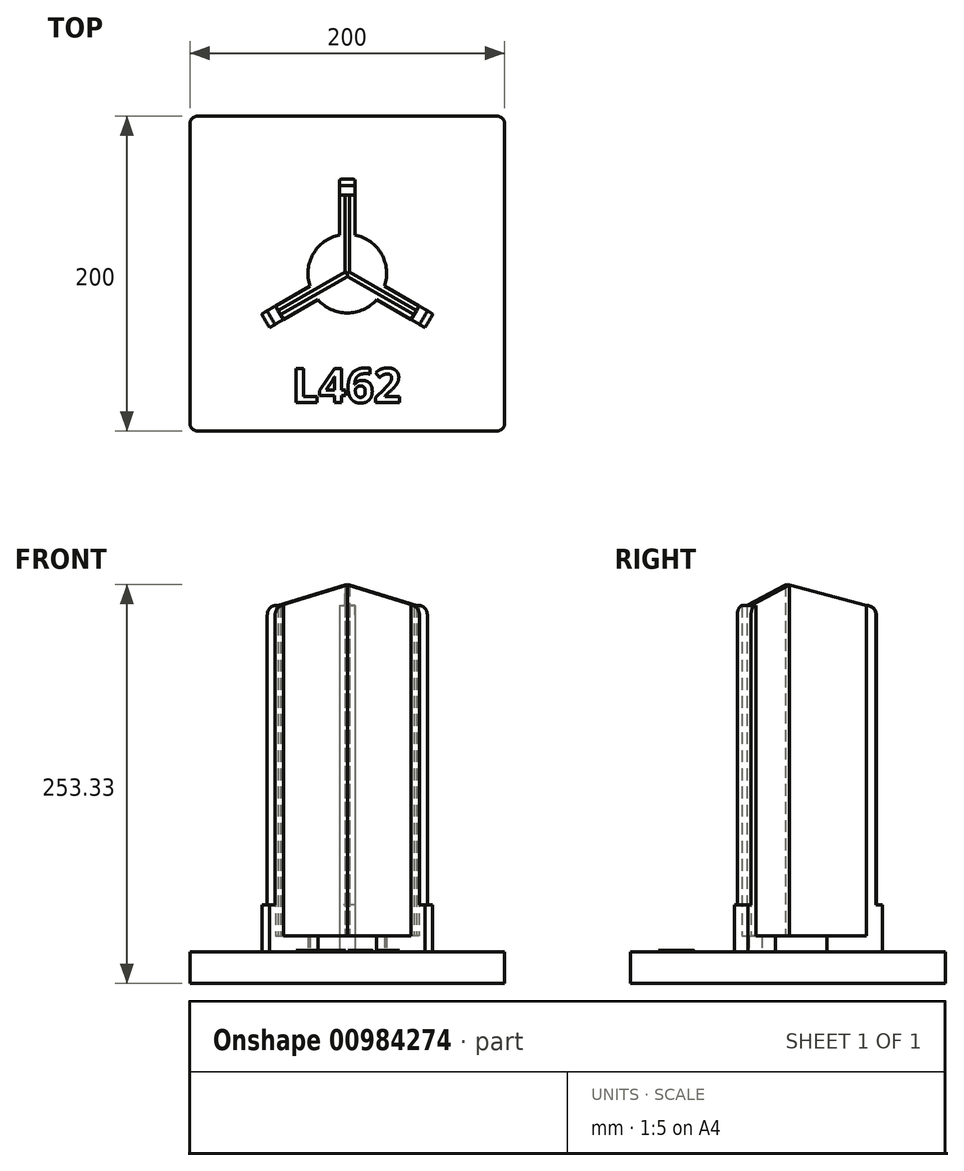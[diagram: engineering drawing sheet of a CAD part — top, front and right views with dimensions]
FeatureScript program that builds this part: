
annotation { "Feature Type Name" : "Feature", "Feature Type Description" : "" }
export const myFeature = defineFeature(function(context is Context, id is Id, definition is map)
    precondition{}
    {
        {
            var Q0;
            Q0=qCreatedBy(makeId("Top.planeOp"),FACE);
            var sketch = newSketch(context, id + "F0", { "sketchPlane" : qUnion([Q0])});
            skCircle(sketch, "E0", {"center": v(0, 0) * mm, "radius": 60 * mm});
            skCircle(sketch, "E1", {"center": v(0, 0) * mm, "radius": 56 * mm});
            skCircle(sketch, "E2", {"center": v(0, 0) * mm, "radius": 25 * mm});
            skLineSegment(sketch, "E3", {"start": v(-1.5, 55.98) * mm, "end": v(1.5, 55.98) * mm, "construction": true});
            skLineSegment(sketch, "E4", {"start": v(-5, 59.8) * mm, "end": v(5, 59.8) * mm, "construction": true});
            skCircle(sketch, "E5", {"center": v(0, 0) * mm, "radius": 1.5 * mm, "construction": true});
            skLineSegment(sketch, "E6", {"start": v(-1.5, 55.98) * mm, "end": v(-1.5, 0) * mm});
            skLineSegment(sketch, "E7", {"start": v(1.5, 55.98) * mm, "end": v(1.5, 0) * mm});
            skLineSegment(sketch, "E8", {"start": v(-5, 59.8) * mm, "end": v(-5, 55.78) * mm});
            skLineSegment(sketch, "E9", {"start": v(5, 59.8) * mm, "end": v(5, 55.78) * mm});
            skLineSegment(sketch, "E10", {"start": v(-1.5, 24.95) * mm, "end": v(-22.36, -11.18) * mm, "construction": true});
            skCircle(sketch, "E11", {"center": v(-11.93, 6.89) * mm, "radius": 3.5 * mm});
            skCircle(sketch, "E12", {"center": v(-11.93, 6.89) * mm, "radius": 1.75 * mm});
            skCircle(sketch, "E13.1.0", {"center": v(0, -13.78) * mm, "radius": 1.75 * mm});
            skCircle(sketch, "E13.1.1", {"center": v(0, -13.78) * mm, "radius": 3.5 * mm});
            skCircle(sketch, "E13.2.0", {"center": v(11.93, 6.89) * mm, "radius": 1.75 * mm});
            skCircle(sketch, "E13.2.1", {"center": v(11.93, 6.89) * mm, "radius": 3.5 * mm});
            skLineSegment(sketch, "E14", {"start": v(-5, 55.78) * mm, "end": v(-5, 24.5) * mm});
            skLineSegment(sketch, "E15", {"start": v(5, 55.78) * mm, "end": v(5, 24.5) * mm});
            skCircle(sketch, "E16", {"center": v(0, 0) * mm, "radius": 50 * mm, "construction": true});
            skLineSegment(sketch, "E17", {"start": v(-5, 49.75) * mm, "end": v(5, 49.75) * mm});
            skLineSegment(sketch, "E18.1.0", {"start": v(-47.73, -29.29) * mm, "end": v(0.75, -1.3) * mm});
            skLineSegment(sketch, "E18.1.1", {"start": v(-49.23, -26.7) * mm, "end": v(-0.75, 1.3) * mm});
            skLineSegment(sketch, "E18.1.2", {"start": v(-45.8, -32.22) * mm, "end": v(-18.71, -16.58) * mm});
            skLineSegment(sketch, "E18.1.3", {"start": v(-50.8, -23.56) * mm, "end": v(-23.71, -7.92) * mm});
            skLineSegment(sketch, "E18.1.4", {"start": v(-49.28, -34.23) * mm, "end": v(-45.8, -32.22) * mm});
            skLineSegment(sketch, "E18.1.5", {"start": v(-54.28, -25.57) * mm, "end": v(-50.8, -23.56) * mm});
            skLineSegment(sketch, "E18.1.6", {"start": v(-49.28, -34.23) * mm, "end": v(-54.28, -25.57) * mm, "construction": true});
            skLineSegment(sketch, "E18.1.7", {"start": v(-47.73, -29.29) * mm, "end": v(-49.23, -26.7) * mm, "construction": true});
            skLineSegment(sketch, "E18.1.8", {"start": v(-40.58, -29.2) * mm, "end": v(-45.58, -20.54) * mm});
            skLineSegment(sketch, "E18.2.0", {"start": v(49.23, -26.7) * mm, "end": v(0.75, 1.3) * mm});
            skLineSegment(sketch, "E18.2.1", {"start": v(47.73, -29.29) * mm, "end": v(-0.75, -1.3) * mm});
            skLineSegment(sketch, "E18.2.2", {"start": v(50.8, -23.56) * mm, "end": v(23.71, -7.92) * mm});
            skLineSegment(sketch, "E18.2.3", {"start": v(45.8, -32.22) * mm, "end": v(18.71, -16.58) * mm});
            skLineSegment(sketch, "E18.2.4", {"start": v(54.28, -25.57) * mm, "end": v(50.8, -23.56) * mm});
            skLineSegment(sketch, "E18.2.5", {"start": v(49.28, -34.23) * mm, "end": v(45.8, -32.22) * mm});
            skLineSegment(sketch, "E18.2.6", {"start": v(54.28, -25.57) * mm, "end": v(49.28, -34.23) * mm, "construction": true});
            skLineSegment(sketch, "E18.2.7", {"start": v(49.23, -26.7) * mm, "end": v(47.73, -29.29) * mm, "construction": true});
            skLineSegment(sketch, "E18.2.8", {"start": v(45.58, -20.54) * mm, "end": v(40.58, -29.2) * mm});
            skText(sketch, "E19", { "text": "L462", "fontName": "OpenSans-Bold.ttf"});
            const initialGuessF0  = {"E19": [-0.0353, -0.082, 1, 0, 0.022]};
            skSetInitialGuess(sketch, initialGuessF0);
            skSolve(sketch);
        }
        {
            var Q0;
            {var subQ0=sQuery(id+"F0.wireOp",EDGE,"E2");var subQ1=sQuery(id+"F0.wireOp",EDGE,"Qz9RoNIK-bmAM-g4SH-EP3c-7Fqs6VSRPzqB.left");var subQ2=makeQuery(id+"F0.imprint","INTERSECT",VERTEX,{"disambiguationData":[OD(0.0)],"derivedFrom":[subQ1,subQ0]});Q0=makeQuery(id+"F0.imprint","IMPRINT",FACE,{"disambiguationData":[TD([[makeQuery(id+"F0.imprint","IMPRINT",EDGE,{"disambiguationData":[TD([[subQ2,-1.0]])],"derivedFrom":subQ1}),1.0]])]});}
            var Q1;
            {var subQ0=sQuery(id+"F0.wireOp",EDGE,"E2");var subQ1=sQuery(id+"F0.wireOp",EDGE,"Qz9RoNIK-bmAM-g4SH-EP3c-7Fqs6VSRPzqB.left");var subQ2=makeQuery(id+"F0.imprint","INTERSECT",VERTEX,{"disambiguationData":[OD(0.0)],"derivedFrom":[subQ1,subQ0]});Q1=makeQuery(id+"F0.imprint","IMPRINT",FACE,{"disambiguationData":[TD([[makeQuery(id+"F0.imprint","IMPRINT",EDGE,{"disambiguationData":[TD([[subQ2,-1.0]])],"derivedFrom":subQ1}),-1.0]])]});}
            var Q2;
            {var subQ1=sQuery(id+"F0.wireOp",EDGE,"Qz9RoNIK-bmAM-g4SH-EP3c-7Fqs6VSRPzqB.right");var subQ5=sQuery(id+"F0.wireOp",EDGE,"E2");var subQ6=makeQuery(id+"F0.imprint","INTERSECT",VERTEX,{"disambiguationData":[OD(0.0)],"derivedFrom":[subQ1,subQ5]});Q2=makeQuery(id+"F0.imprint","IMPRINT",FACE,{"disambiguationData":[TD([[makeQuery(id+"F0.imprint","IMPRINT",EDGE,{"disambiguationData":[TD([[subQ6,-1.0]])],"derivedFrom":subQ1}),-1.0]])]});}
            var Q3;
            {var subQ5=sQuery(id+"F0.wireOp",EDGE,"Qz9RoNIK-bmAM-g4SH-EP3c-7Fqs6VSRPzqB.right");var subQ7=sQuery(id+"F0.wireOp",EDGE,"I0Sq5aEr-Hngn-Fm4D-tp8S-rX2HjxpjUaP6.bottom");var subQ8=makeQuery(id+"F0.imprint","INTERSECT",VERTEX,{"derivedFrom":[subQ5,subQ7]});Q3=makeQuery(id+"F0.imprint","IMPRINT",FACE,{"disambiguationData":[TD([[makeQuery(id+"F0.imprint","IMPRINT",EDGE,{"disambiguationData":[TD([[subQ8,-1.0]])],"derivedFrom":subQ5}),-1.0]])]});}
            var Q4;
            {var subQ0=sQuery(id+"F0.wireOp",EDGE,"I0Sq5aEr-Hngn-Fm4D-tp8S-rX2HjxpjUaP6.bottom");var subQ1=sQuery(id+"F0.wireOp",EDGE,"Qz9RoNIK-bmAM-g4SH-EP3c-7Fqs6VSRPzqB.left");var subQ2=makeQuery(id+"F0.imprint","INTERSECT",VERTEX,{"derivedFrom":[subQ1,subQ0]});Q4=makeQuery(id+"F0.imprint","IMPRINT",FACE,{"disambiguationData":[TD([[makeQuery(id+"F0.imprint","IMPRINT",EDGE,{"disambiguationData":[TD([[subQ2,-1.0]])],"derivedFrom":subQ1}),-1.0]])]});}
            var Q5;
            {var subQ5=sQuery(id+"F0.wireOp",EDGE,"Qz9RoNIK-bmAM-g4SH-EP3c-7Fqs6VSRPzqB.left");var subQ7=sQuery(id+"F0.wireOp",EDGE,"I0Sq5aEr-Hngn-Fm4D-tp8S-rX2HjxpjUaP6.bottom");var subQ8=makeQuery(id+"F0.imprint","INTERSECT",VERTEX,{"derivedFrom":[subQ5,subQ7]});Q5=makeQuery(id+"F0.imprint","IMPRINT",FACE,{"disambiguationData":[TD([[makeQuery(id+"F0.imprint","IMPRINT",EDGE,{"disambiguationData":[TD([[subQ8,-1.0]])],"derivedFrom":subQ5}),1.0]])]});}
            var Q6;
            {var subQ0=sQuery(id+"F0.wireOp",EDGE,"MHhcaKt2-idaq-ussF-yxv1-Ysw6X7YejIML.top");var subQ1=sQuery(id+"F0.wireOp",EDGE,"Qz9RoNIK-bmAM-g4SH-EP3c-7Fqs6VSRPzqB.left");var subQ2=makeQuery(id+"F0.imprint","INTERSECT",VERTEX,{"derivedFrom":[subQ1,subQ0]});Q6=makeQuery(id+"F0.imprint","IMPRINT",FACE,{"disambiguationData":[TD([[makeQuery(id+"F0.imprint","IMPRINT",EDGE,{"disambiguationData":[TD([[subQ2,-1.0]])],"derivedFrom":subQ1}),1.0]])]});}
            var Q7;
            {var subQ0=sQuery(id+"F0.wireOp",EDGE,"MHhcaKt2-idaq-ussF-yxv1-Ysw6X7YejIML.top");var subQ1=sQuery(id+"F0.wireOp",EDGE,"Qz9RoNIK-bmAM-g4SH-EP3c-7Fqs6VSRPzqB.left");var subQ2=makeQuery(id+"F0.imprint","INTERSECT",VERTEX,{"derivedFrom":[subQ1,subQ0]});Q7=makeQuery(id+"F0.imprint","IMPRINT",FACE,{"disambiguationData":[TD([[makeQuery(id+"F0.imprint","IMPRINT",EDGE,{"disambiguationData":[TD([[subQ2,-1.0]])],"derivedFrom":subQ1}),-1.0]])]});}
            var Q8;
            {var subQ0=sQuery(id+"F0.wireOp",EDGE,"MHhcaKt2-idaq-ussF-yxv1-Ysw6X7YejIML.top");var subQ1=sQuery(id+"F0.wireOp",EDGE,"Qz9RoNIK-bmAM-g4SH-EP3c-7Fqs6VSRPzqB.right");var subQ2=makeQuery(id+"F0.imprint","INTERSECT",VERTEX,{"derivedFrom":[subQ1,subQ0]});Q8=makeQuery(id+"F0.imprint","IMPRINT",FACE,{"disambiguationData":[TD([[makeQuery(id+"F0.imprint","IMPRINT",EDGE,{"disambiguationData":[TD([[subQ2,-1.0]])],"derivedFrom":subQ1}),-1.0]])]});}
            var Q9;
            {var subQ0=sQuery(id+"F0.wireOp",EDGE,"I0Sq5aEr-Hngn-Fm4D-tp8S-rX2HjxpjUaP6.right");var subQ1=sQuery(id+"F0.wireOp",EDGE,"MHhcaKt2-idaq-ussF-yxv1-Ysw6X7YejIML.bottom");var subQ2=makeQuery(id+"F0.imprint","INTERSECT",VERTEX,{"derivedFrom":[subQ1,subQ0]});Q9=makeQuery(id+"F0.imprint","IMPRINT",FACE,{"disambiguationData":[TD([[makeQuery(id+"F0.imprint","IMPRINT",EDGE,{"disambiguationData":[TD([[subQ2,-1.0]])],"derivedFrom":subQ1}),-1.0]])]});}
            var Q10;
            {var subQ0=sQuery(id+"F0.wireOp",EDGE,"I0Sq5aEr-Hngn-Fm4D-tp8S-rX2HjxpjUaP6.top");var subQ1=sQuery(id+"F0.wireOp",EDGE,"Qz9RoNIK-bmAM-g4SH-EP3c-7Fqs6VSRPzqB.right");var subQ2=makeQuery(id+"F0.imprint","INTERSECT",VERTEX,{"derivedFrom":[subQ1,subQ0]});Q10=makeQuery(id+"F0.imprint","IMPRINT",FACE,{"disambiguationData":[TD([[makeQuery(id+"F0.imprint","IMPRINT",EDGE,{"disambiguationData":[TD([[subQ2,-1.0]])],"derivedFrom":subQ1}),-1.0]])]});}
            var Q11;
            {var subQ1=sQuery(id+"F0.wireOp",EDGE,"MHhcaKt2-idaq-ussF-yxv1-Ysw6X7YejIML.bottom");var subQ7=sQuery(id+"F0.wireOp",EDGE,"Qz9RoNIK-bmAM-g4SH-EP3c-7Fqs6VSRPzqB.right");var subQ8=makeQuery(id+"F0.imprint","INTERSECT",VERTEX,{"derivedFrom":[subQ7,subQ1]});Q11=makeQuery(id+"F0.imprint","IMPRINT",FACE,{"disambiguationData":[TD([[makeQuery(id+"F0.imprint","IMPRINT",EDGE,{"disambiguationData":[TD([[subQ8,-1.0]])],"derivedFrom":subQ7}),-1.0]])]});}
            var Q12;
            {var subQ0=sQuery(id+"F0.wireOp",EDGE,"MHhcaKt2-idaq-ussF-yxv1-Ysw6X7YejIML.bottom");var subQ1=sQuery(id+"F0.wireOp",EDGE,"Qz9RoNIK-bmAM-g4SH-EP3c-7Fqs6VSRPzqB.left");var subQ2=makeQuery(id+"F0.imprint","INTERSECT",VERTEX,{"derivedFrom":[subQ1,subQ0]});Q12=makeQuery(id+"F0.imprint","IMPRINT",FACE,{"disambiguationData":[TD([[makeQuery(id+"F0.imprint","IMPRINT",EDGE,{"disambiguationData":[TD([[subQ2,-1.0]])],"derivedFrom":subQ1}),-1.0]])]});}
            var Q13;
            {var subQ1=sQuery(id+"F0.wireOp",EDGE,"MHhcaKt2-idaq-ussF-yxv1-Ysw6X7YejIML.bottom");var subQ7=sQuery(id+"F0.wireOp",EDGE,"Qz9RoNIK-bmAM-g4SH-EP3c-7Fqs6VSRPzqB.left");var subQ8=makeQuery(id+"F0.imprint","INTERSECT",VERTEX,{"derivedFrom":[subQ7,subQ1]});Q13=makeQuery(id+"F0.imprint","IMPRINT",FACE,{"disambiguationData":[TD([[makeQuery(id+"F0.imprint","IMPRINT",EDGE,{"disambiguationData":[TD([[subQ8,-1.0]])],"derivedFrom":subQ7}),1.0]])]});}
            var Q14;
            {var subQ0=sQuery(id+"F0.wireOp",EDGE,"I0Sq5aEr-Hngn-Fm4D-tp8S-rX2HjxpjUaP6.top");var subQ1=sQuery(id+"F0.wireOp",EDGE,"Qz9RoNIK-bmAM-g4SH-EP3c-7Fqs6VSRPzqB.left");var subQ2=makeQuery(id+"F0.imprint","INTERSECT",VERTEX,{"derivedFrom":[subQ1,subQ0]});Q14=makeQuery(id+"F0.imprint","IMPRINT",FACE,{"disambiguationData":[TD([[makeQuery(id+"F0.imprint","IMPRINT",EDGE,{"disambiguationData":[TD([[subQ2,-1.0]])],"derivedFrom":subQ1}),1.0]])]});}
            var Q15;
            {var subQ0=sQuery(id+"F0.wireOp",EDGE,"E2");var subQ1=sQuery(id+"F0.wireOp",EDGE,"MHhcaKt2-idaq-ussF-yxv1-Ysw6X7YejIML.bottom");var subQ2=makeQuery(id+"F0.imprint","INTERSECT",VERTEX,{"disambiguationData":[OD(0.0)],"derivedFrom":[subQ1,subQ0]});Q15=makeQuery(id+"F0.imprint","IMPRINT",FACE,{"disambiguationData":[TD([[makeQuery(id+"F0.imprint","IMPRINT",EDGE,{"disambiguationData":[TD([[subQ2,-1.0]])],"derivedFrom":subQ1}),-1.0]])]});}
            var Q16;
            {var subQ0=sQuery(id+"F0.wireOp",EDGE,"I0Sq5aEr-Hngn-Fm4D-tp8S-rX2HjxpjUaP6.top");var subQ1=sQuery(id+"F0.wireOp",EDGE,"Qz9RoNIK-bmAM-g4SH-EP3c-7Fqs6VSRPzqB.left");var subQ2=makeQuery(id+"F0.imprint","INTERSECT",VERTEX,{"derivedFrom":[subQ1,subQ0]});Q16=makeQuery(id+"F0.imprint","IMPRINT",FACE,{"disambiguationData":[TD([[makeQuery(id+"F0.imprint","IMPRINT",EDGE,{"disambiguationData":[TD([[subQ2,-1.0]])],"derivedFrom":subQ1}),-1.0]])]});}
            var Q17;
            {var subQ0=sQuery(id+"F0.wireOp",EDGE,"ARnEnpE5-tkmW-Q9Fp-N7HQ-ZdpaRJQSmeqH.top");Q17=makeQuery(id+"F0.imprint","IMPRINT",FACE,{"disambiguationData":[TD([[makeQuery(id+"F0.imprint","IMPRINT",EDGE,{"derivedFrom":subQ0}),1.0]])]});}
            var Q18;
            {var subQ0=sQuery(id+"F0.wireOp",EDGE,"fYTYB3PY-5dvC-i0FG-IhBz-imLdNv0oFj73.right");Q18=makeQuery(id+"F0.imprint","IMPRINT",FACE,{"disambiguationData":[TD([[makeQuery(id+"F0.imprint","IMPRINT",EDGE,{"derivedFrom":subQ0}),-1.0]])]});}
            var Q19;
            {var subQ0=sQuery(id+"F0.wireOp",EDGE,"JRACFuVa-LFQl-MoOF-o5kD-FoGYgOgg0vGQ.top");Q19=makeQuery(id+"F0.imprint","IMPRINT",FACE,{"disambiguationData":[TD([[makeQuery(id+"F0.imprint","IMPRINT",EDGE,{"derivedFrom":subQ0}),-1.0]])]});}
            var Q20;
            {var subQ0=sQuery(id+"F0.wireOp",EDGE,"qvxIDn41-u5vC-3tcf-A1ba-gfAf9TCSAjBw.right");Q20=makeQuery(id+"F0.imprint","IMPRINT",FACE,{"disambiguationData":[TD([[makeQuery(id+"F0.imprint","IMPRINT",EDGE,{"derivedFrom":subQ0}),1.0]])]});}
            var Q21;
            {var subQ0=sQuery(id+"F0.wireOp",EDGE,"E2");var subQ1=sQuery(id+"F0.wireOp",EDGE,"Qz9RoNIK-bmAM-g4SH-EP3c-7Fqs6VSRPzqB.right");var subQ2=makeQuery(id+"F0.imprint","INTERSECT",VERTEX,{"disambiguationData":[OD(0.0)],"derivedFrom":[subQ1,subQ0]});Q21=makeQuery(id+"F0.imprint","IMPRINT",FACE,{"disambiguationData":[TD([[makeQuery(id+"F0.imprint","IMPRINT",EDGE,{"disambiguationData":[TD([[subQ2,-1.0]])],"derivedFrom":subQ1}),1.0]])]});}
            var Q22;
            {var subQ0=sQuery(id+"F0.wireOp",EDGE,"I0Sq5aEr-Hngn-Fm4D-tp8S-rX2HjxpjUaP6.bottom");var subQ1=sQuery(id+"F0.wireOp",EDGE,"Qz9RoNIK-bmAM-g4SH-EP3c-7Fqs6VSRPzqB.right");var subQ2=makeQuery(id+"F0.imprint","INTERSECT",VERTEX,{"derivedFrom":[subQ1,subQ0]});Q22=makeQuery(id+"F0.imprint","IMPRINT",FACE,{"disambiguationData":[TD([[makeQuery(id+"F0.imprint","IMPRINT",EDGE,{"disambiguationData":[TD([[subQ2,-1.0]])],"derivedFrom":subQ1}),1.0]])]});}
            var Q23;
            {var subQ0=sQuery(id+"F0.wireOp",EDGE,"MHhcaKt2-idaq-ussF-yxv1-Ysw6X7YejIML.top");var subQ1=sQuery(id+"F0.wireOp",EDGE,"Qz9RoNIK-bmAM-g4SH-EP3c-7Fqs6VSRPzqB.right");var subQ2=makeQuery(id+"F0.imprint","INTERSECT",VERTEX,{"derivedFrom":[subQ1,subQ0]});Q23=makeQuery(id+"F0.imprint","IMPRINT",FACE,{"disambiguationData":[TD([[makeQuery(id+"F0.imprint","IMPRINT",EDGE,{"disambiguationData":[TD([[subQ2,-1.0]])],"derivedFrom":subQ1}),1.0]])]});}
            var Q24;
            {var subQ0=sQuery(id+"F0.wireOp",EDGE,"I0Sq5aEr-Hngn-Fm4D-tp8S-rX2HjxpjUaP6.right");var subQ1=sQuery(id+"F0.wireOp",EDGE,"MHhcaKt2-idaq-ussF-yxv1-Ysw6X7YejIML.top");var subQ2=makeQuery(id+"F0.imprint","INTERSECT",VERTEX,{"derivedFrom":[subQ1,subQ0]});Q24=makeQuery(id+"F0.imprint","IMPRINT",FACE,{"disambiguationData":[TD([[makeQuery(id+"F0.imprint","IMPRINT",EDGE,{"disambiguationData":[TD([[subQ2,-1.0]])],"derivedFrom":subQ1}),1.0]])]});}
            var Q25;
            {var subQ0=sQuery(id+"F0.wireOp",EDGE,"MHhcaKt2-idaq-ussF-yxv1-Ysw6X7YejIML.bottom");var subQ1=sQuery(id+"F0.wireOp",EDGE,"Qz9RoNIK-bmAM-g4SH-EP3c-7Fqs6VSRPzqB.right");var subQ2=makeQuery(id+"F0.imprint","INTERSECT",VERTEX,{"derivedFrom":[subQ1,subQ0]});Q25=makeQuery(id+"F0.imprint","IMPRINT",FACE,{"disambiguationData":[TD([[makeQuery(id+"F0.imprint","IMPRINT",EDGE,{"disambiguationData":[TD([[subQ2,-1.0]])],"derivedFrom":subQ1}),1.0]])]});}
            var Q26;
            {var subQ0=sQuery(id+"F0.wireOp",EDGE,"I0Sq5aEr-Hngn-Fm4D-tp8S-rX2HjxpjUaP6.top");var subQ1=sQuery(id+"F0.wireOp",EDGE,"Qz9RoNIK-bmAM-g4SH-EP3c-7Fqs6VSRPzqB.right");var subQ2=makeQuery(id+"F0.imprint","INTERSECT",VERTEX,{"derivedFrom":[subQ1,subQ0]});Q26=makeQuery(id+"F0.imprint","IMPRINT",FACE,{"disambiguationData":[TD([[makeQuery(id+"F0.imprint","IMPRINT",EDGE,{"disambiguationData":[TD([[subQ2,-1.0]])],"derivedFrom":subQ1}),1.0]])]});}
            var Q27;
            {var subQ0=sQuery(id+"F0.wireOp",EDGE,"UooLEnTI-Uf4f-MH2r-6JwD-Mf36DO2BtYOc.top");var subQ1=sQuery(id+"F0.wireOp",EDGE,"Qz9RoNIK-bmAM-g4SH-EP3c-7Fqs6VSRPzqB.right");var subQ2=makeQuery(id+"F0.imprint","INTERSECT",VERTEX,{"derivedFrom":[subQ1,subQ0]});Q27=makeQuery(id+"F0.imprint","IMPRINT",FACE,{"disambiguationData":[TD([[makeQuery(id+"F0.imprint","IMPRINT",EDGE,{"disambiguationData":[TD([[subQ2,-1.0]])],"derivedFrom":subQ1}),-1.0]])]});}
            var Q28;
            {var subQ0=sQuery(id+"F0.wireOp",EDGE,"UooLEnTI-Uf4f-MH2r-6JwD-Mf36DO2BtYOc.top");var subQ1=sQuery(id+"F0.wireOp",EDGE,"Qz9RoNIK-bmAM-g4SH-EP3c-7Fqs6VSRPzqB.right");var subQ2=makeQuery(id+"F0.imprint","INTERSECT",VERTEX,{"derivedFrom":[subQ1,subQ0]});Q28=makeQuery(id+"F0.imprint","IMPRINT",FACE,{"disambiguationData":[TD([[makeQuery(id+"F0.imprint","IMPRINT",EDGE,{"disambiguationData":[TD([[subQ2,-1.0]])],"derivedFrom":subQ1}),1.0]])]});}
            var Q29;
            {var subQ0=sQuery(id+"F0.wireOp",EDGE,"UooLEnTI-Uf4f-MH2r-6JwD-Mf36DO2BtYOc.top");var subQ1=sQuery(id+"F0.wireOp",EDGE,"Qz9RoNIK-bmAM-g4SH-EP3c-7Fqs6VSRPzqB.left");var subQ2=makeQuery(id+"F0.imprint","INTERSECT",VERTEX,{"derivedFrom":[subQ1,subQ0]});Q29=makeQuery(id+"F0.imprint","IMPRINT",FACE,{"disambiguationData":[TD([[makeQuery(id+"F0.imprint","IMPRINT",EDGE,{"disambiguationData":[TD([[subQ2,-1.0]])],"derivedFrom":subQ1}),-1.0]])]});}
            var Q30;
            {var subQ0=sQuery(id+"F0.wireOp",EDGE,"UooLEnTI-Uf4f-MH2r-6JwD-Mf36DO2BtYOc.top");var subQ1=sQuery(id+"F0.wireOp",EDGE,"Qz9RoNIK-bmAM-g4SH-EP3c-7Fqs6VSRPzqB.left");var subQ2=makeQuery(id+"F0.imprint","INTERSECT",VERTEX,{"derivedFrom":[subQ1,subQ0]});Q30=makeQuery(id+"F0.imprint","IMPRINT",FACE,{"disambiguationData":[TD([[makeQuery(id+"F0.imprint","IMPRINT",EDGE,{"disambiguationData":[TD([[subQ2,-1.0]])],"derivedFrom":subQ1}),1.0]])]});}
            var Q31;
            {var subQ0=sQuery(id+"F0.wireOp",EDGE,"E2");var subQ1=sQuery(id+"F0.wireOp",EDGE,"MHhcaKt2-idaq-ussF-yxv1-Ysw6X7YejIML.top");var subQ2=makeQuery(id+"F0.imprint","INTERSECT",VERTEX,{"disambiguationData":[OD(0.0)],"derivedFrom":[subQ1,subQ0]});Q31=makeQuery(id+"F0.imprint","IMPRINT",FACE,{"disambiguationData":[TD([[makeQuery(id+"F0.imprint","IMPRINT",EDGE,{"disambiguationData":[TD([[subQ2,-1.0]])],"derivedFrom":subQ1}),1.0]])]});}
            var Q32;
            {var subQ0=sQuery(id+"F0.wireOp",EDGE,"UaoCu7b1-m9SB-61mE-joAU-4Tf4ClvXxRAN");var subQ4=sQuery(id+"F0.wireOp",EDGE,"Z93t4qtu-qqve-2JoU-aCnr-fMp0EEGuzRtp");var subQ5=makeQuery(id+"F0.imprint","INTERSECT",VERTEX,{"disambiguationData":[OD(0.0)],"derivedFrom":[subQ4,subQ0]});Q32=makeQuery(id+"F0.imprint","IMPRINT",FACE,{"disambiguationData":[TD([[makeQuery(id+"F0.imprint","IMPRINT",EDGE,{"disambiguationData":[TD([[subQ5,1.0]])],"derivedFrom":subQ4}),-1.0]])]});}
            var Q33;
            Q33=makeQuery(id+"F0.imprint","IMPRINT",FACE,{"disambiguationData":[TD([[makeQuery(id+"F0.imprint","IMPRINT",EDGE,{"derivedFrom":sQuery(id+"F0.wireOp",EDGE,"3ba069c8-a511-4e33-be52-923c701046d1.1.1")}),-1.0]])]});
            var Q34;
            {var subQ5=sQuery(id+"F0.wireOp",EDGE,"3ec345ef-f0f0-4e93-9e5e-b6a35eb55933.1.2");var subQ6=sQuery(id+"F0.wireOp",EDGE,"E2");var subQ7=makeQuery(id+"F0.imprint","INTERSECT",VERTEX,{"derivedFrom":[subQ6,subQ5]});Q34=makeQuery(id+"F0.imprint","IMPRINT",FACE,{"disambiguationData":[TD([[makeQuery(id+"F0.imprint","IMPRINT",EDGE,{"disambiguationData":[TD([[subQ7,-1.0]])],"derivedFrom":subQ6}),1.0]])]});}
            var Q35;
            {var subQ1=sQuery(id+"F0.wireOp",EDGE,"E2");var subQ7=sQuery(id+"F0.wireOp",EDGE,"3ec345ef-f0f0-4e93-9e5e-b6a35eb55933.2.6");var subQ9=makeQuery(id+"F0.imprint","INTERSECT",VERTEX,{"derivedFrom":[subQ1,subQ7]});Q35=makeQuery(id+"F0.imprint","IMPRINT",FACE,{"disambiguationData":[TD([[makeQuery(id+"F0.imprint","IMPRINT",EDGE,{"disambiguationData":[TD([[subQ9,-1.0]])],"derivedFrom":subQ1}),1.0]])]});}
            var Q36;
            {var subQ1=sQuery(id+"F0.wireOp",EDGE,"Qz9RoNIK-bmAM-g4SH-EP3c-7Fqs6VSRPzqB.left");var subQ5=sQuery(id+"F0.wireOp",EDGE,"Fhyrr48q-6Ub6-qUJE-WvSH-lKAYv9wGpefs");var subQ6=makeQuery(id+"F0.imprint","INTERSECT",VERTEX,{"derivedFrom":[subQ1,subQ5]});Q36=makeQuery(id+"F0.imprint","IMPRINT",FACE,{"disambiguationData":[TD([[makeQuery(id+"F0.imprint","IMPRINT",EDGE,{"disambiguationData":[TD([[subQ6,1.0]])],"derivedFrom":subQ1}),1.0]])]});}
            var Q37;
            {var subQ0=sQuery(id+"F0.wireOp",EDGE,"Fhyrr48q-6Ub6-qUJE-WvSH-lKAYv9wGpefs");var subQ1=sQuery(id+"F0.wireOp",EDGE,"Qz9RoNIK-bmAM-g4SH-EP3c-7Fqs6VSRPzqB.left");var subQ2=makeQuery(id+"F0.imprint","INTERSECT",VERTEX,{"derivedFrom":[subQ1,subQ0]});Q37=makeQuery(id+"F0.imprint","IMPRINT",FACE,{"disambiguationData":[TD([[makeQuery(id+"F0.imprint","IMPRINT",EDGE,{"disambiguationData":[TD([[subQ2,1.0]])],"derivedFrom":subQ1}),-1.0]])]});}
            var Q38;
            {var subQ3=sQuery(id+"F0.wireOp",EDGE,"3ec345ef-f0f0-4e93-9e5e-b6a35eb55933.1.15");var subQ7=sQuery(id+"F0.wireOp",EDGE,"3ec345ef-f0f0-4e93-9e5e-b6a35eb55933.1.0");var subQ8=makeQuery(id+"F0.imprint","INTERSECT",VERTEX,{"derivedFrom":[subQ7,subQ3]});Q38=makeQuery(id+"F0.imprint","IMPRINT",FACE,{"disambiguationData":[TD([[makeQuery(id+"F0.imprint","IMPRINT",EDGE,{"disambiguationData":[TD([[subQ8,1.0]])],"derivedFrom":subQ7}),1.0]])]});}
            var Q39;
            {var subQ0=sQuery(id+"F0.wireOp",EDGE,"15ffb876-a102-4fbe-8a3e-136bf1afb38e.1.1");Q39=makeQuery(id+"F0.imprint","IMPRINT",FACE,{"disambiguationData":[TD([[makeQuery(id+"F0.imprint","IMPRINT",EDGE,{"derivedFrom":subQ0}),-1.0]])]});}
            var Q40;
            {var subQ3=sQuery(id+"F0.wireOp",EDGE,"15ffb876-a102-4fbe-8a3e-136bf1afb38e.1.4");Q40=makeQuery(id+"F0.imprint","IMPRINT",FACE,{"disambiguationData":[TD([[makeQuery(id+"F0.imprint","IMPRINT",EDGE,{"derivedFrom":subQ3}),1.0]])]});}
            var Q41;
            {var subQ0=sQuery(id+"F0.wireOp",EDGE,"15ffb876-a102-4fbe-8a3e-136bf1afb38e.2.1");Q41=makeQuery(id+"F0.imprint","IMPRINT",FACE,{"disambiguationData":[TD([[makeQuery(id+"F0.imprint","IMPRINT",EDGE,{"derivedFrom":subQ0}),-1.0]])]});}
            var Q42;
            {var subQ3=sQuery(id+"F0.wireOp",EDGE,"15ffb876-a102-4fbe-8a3e-136bf1afb38e.2.4");Q42=makeQuery(id+"F0.imprint","IMPRINT",FACE,{"disambiguationData":[TD([[makeQuery(id+"F0.imprint","IMPRINT",EDGE,{"derivedFrom":subQ3}),1.0]])]});}
            var Q43;
            {var subQ0=sQuery(id+"F0.wireOp",EDGE,"E18.1.3");var subQ1=sQuery(id+"F0.wireOp",EDGE,"E2");var subQ2=makeQuery(id+"F0.imprint","INTERSECT",VERTEX,{"derivedFrom":[subQ1,subQ0]});Q43=makeQuery(id+"F0.imprint","IMPRINT",FACE,{"disambiguationData":[TD([[makeQuery(id+"F0.imprint","IMPRINT",EDGE,{"disambiguationData":[TD([[subQ2,-1.0]])],"derivedFrom":subQ1}),-1.0]])]});}
            var Q44;
            {var subQ0=sQuery(id+"F0.wireOp",EDGE,"E18.1.2");var subQ1=sQuery(id+"F0.wireOp",EDGE,"E2");var subQ2=makeQuery(id+"F0.imprint","INTERSECT",VERTEX,{"derivedFrom":[subQ1,subQ0]});Q44=makeQuery(id+"F0.imprint","IMPRINT",FACE,{"disambiguationData":[TD([[makeQuery(id+"F0.imprint","IMPRINT",EDGE,{"disambiguationData":[TD([[subQ2,1.0]])],"derivedFrom":subQ1}),-1.0]])]});}
            var Q45;
            {var subQ0=sQuery(id+"F0.wireOp",EDGE,"E18.2.3");var subQ1=sQuery(id+"F0.wireOp",EDGE,"E2");var subQ2=makeQuery(id+"F0.imprint","INTERSECT",VERTEX,{"derivedFrom":[subQ1,subQ0]});Q45=makeQuery(id+"F0.imprint","IMPRINT",FACE,{"disambiguationData":[TD([[makeQuery(id+"F0.imprint","IMPRINT",EDGE,{"disambiguationData":[TD([[subQ2,-1.0]])],"derivedFrom":subQ1}),-1.0]])]});}
            var Q46;
            {var subQ0=sQuery(id+"F0.wireOp",EDGE,"E18.2.2");var subQ1=sQuery(id+"F0.wireOp",EDGE,"E2");var subQ2=makeQuery(id+"F0.imprint","INTERSECT",VERTEX,{"derivedFrom":[subQ1,subQ0]});Q46=makeQuery(id+"F0.imprint","IMPRINT",FACE,{"disambiguationData":[TD([[makeQuery(id+"F0.imprint","IMPRINT",EDGE,{"disambiguationData":[TD([[subQ2,1.0]])],"derivedFrom":subQ1}),-1.0]])]});}
            var Q47;
            {var subQ0=sQuery(id+"F0.wireOp",EDGE,"E14");var subQ1=sQuery(id+"F0.wireOp",EDGE,"E2");var subQ2=makeQuery(id+"F0.imprint","INTERSECT",VERTEX,{"derivedFrom":[subQ1,subQ0]});Q47=makeQuery(id+"F0.imprint","IMPRINT",FACE,{"disambiguationData":[TD([[makeQuery(id+"F0.imprint","IMPRINT",EDGE,{"disambiguationData":[TD([[subQ2,1.0]])],"derivedFrom":subQ1}),-1.0]])]});}
            var Q48;
            {var subQ0=sQuery(id+"F0.wireOp",EDGE,"E15");var subQ1=sQuery(id+"F0.wireOp",EDGE,"E2");var subQ2=makeQuery(id+"F0.imprint","INTERSECT",VERTEX,{"derivedFrom":[subQ1,subQ0]});Q48=makeQuery(id+"F0.imprint","IMPRINT",FACE,{"disambiguationData":[TD([[makeQuery(id+"F0.imprint","IMPRINT",EDGE,{"disambiguationData":[TD([[subQ2,-1.0]])],"derivedFrom":subQ1}),-1.0]])]});}
            var Q49;
            Q49=makeQuery(id+"F0.imprint","IMPRINT",FACE,{"disambiguationData":[TD([[makeQuery(id+"F0.imprint","IMPRINT",EDGE,{"derivedFrom":sQuery(id+"F0.wireOp",EDGE,"E13.2.0")}),-1.0]])]});
            var Q50;
            Q50=makeQuery(id+"F0.imprint","IMPRINT",FACE,{"disambiguationData":[TD([[makeQuery(id+"F0.imprint","IMPRINT",EDGE,{"derivedFrom":sQuery(id+"F0.wireOp",EDGE,"E13.2.0")}),1.0]])]});
            var Q51;
            Q51=makeQuery(id+"F0.imprint","IMPRINT",FACE,{"disambiguationData":[TD([[makeQuery(id+"F0.imprint","IMPRINT",EDGE,{"derivedFrom":sQuery(id+"F0.wireOp",EDGE,"E12")}),1.0]])]});
            var Q52;
            Q52=makeQuery(id+"F0.imprint","IMPRINT",FACE,{"disambiguationData":[TD([[makeQuery(id+"F0.imprint","IMPRINT",EDGE,{"derivedFrom":sQuery(id+"F0.wireOp",EDGE,"E11")}),1.0]])]});
            var Q53;
            Q53=makeQuery(id+"F0.imprint","IMPRINT",FACE,{"disambiguationData":[TD([[makeQuery(id+"F0.imprint","IMPRINT",EDGE,{"derivedFrom":sQuery(id+"F0.wireOp",EDGE,"E13.1.0")}),-1.0]])]});
            var Q54;
            Q54=makeQuery(id+"F0.imprint","IMPRINT",FACE,{"disambiguationData":[TD([[makeQuery(id+"F0.imprint","IMPRINT",EDGE,{"derivedFrom":sQuery(id+"F0.wireOp",EDGE,"E13.1.0")}),1.0]])]});
            extrude(context, id + "F1", {"entities" : qUnion([Q0, Q1, Q2, Q3, Q4, Q5, Q6, Q7, Q8, Q9, Q10, Q11, Q12, Q13, Q14, Q15, Q16, Q17, Q18, Q19, Q20, Q21, Q22, Q23, Q24, Q25, Q26, Q27, Q28, Q29, Q30, Q31, Q32, Q33, Q34, Q35, Q36, Q37, Q38, Q39, Q40, Q41, Q42, Q43, Q44, Q45, Q46, Q47, Q48, Q49, Q50, Q51, Q52, Q53, Q54]), "depth" : 10 * mm, "offsetDistance" : 25 * mm});
        }
        {
            var Q0;
            {var subQ0=sQuery(id+"F0.wireOp",EDGE,"E7");var subQ1=sQuery(id+"F0.wireOp",EDGE,"E1");var subQ2=makeQuery(id+"F0.imprint","INTERSECT",VERTEX,{"derivedFrom":[subQ1,subQ0]});Q0=makeQuery(id+"F0.imprint","IMPRINT",FACE,{"disambiguationData":[TD([[makeQuery(id+"F0.imprint","IMPRINT",EDGE,{"disambiguationData":[TD([[subQ2,-1.0]])],"derivedFrom":subQ0}),1.0]])]});}
            var Q1;
            {var subQ0=sQuery(id+"F0.wireOp",EDGE,"E6");var subQ1=sQuery(id+"F0.wireOp",EDGE,"E1");var subQ2=makeQuery(id+"F0.imprint","INTERSECT",VERTEX,{"derivedFrom":[subQ1,subQ0]});Q1=makeQuery(id+"F0.imprint","IMPRINT",FACE,{"disambiguationData":[TD([[makeQuery(id+"F0.imprint","IMPRINT",EDGE,{"disambiguationData":[TD([[subQ2,-1.0]])],"derivedFrom":subQ0}),-1.0]])]});}
            var Q2;
            {var subQ0=sQuery(id+"F0.wireOp",EDGE,"E18.1.0");var subQ1=sQuery(id+"F0.wireOp",EDGE,"E1");var subQ2=makeQuery(id+"F0.imprint","INTERSECT",VERTEX,{"derivedFrom":[subQ1,subQ0]});Q2=makeQuery(id+"F0.imprint","IMPRINT",FACE,{"disambiguationData":[TD([[makeQuery(id+"F0.imprint","IMPRINT",EDGE,{"disambiguationData":[TD([[subQ2,-1.0]])],"derivedFrom":subQ0}),-1.0]])]});}
            var Q3;
            {var subQ0=sQuery(id+"F0.wireOp",EDGE,"E18.1.1");var subQ1=sQuery(id+"F0.wireOp",EDGE,"E1");var subQ2=makeQuery(id+"F0.imprint","INTERSECT",VERTEX,{"derivedFrom":[subQ1,subQ0]});Q3=makeQuery(id+"F0.imprint","IMPRINT",FACE,{"disambiguationData":[TD([[makeQuery(id+"F0.imprint","IMPRINT",EDGE,{"disambiguationData":[TD([[subQ2,-1.0]])],"derivedFrom":subQ0}),1.0]])]});}
            var Q4;
            {var subQ0=sQuery(id+"F0.wireOp",EDGE,"E18.2.1");var subQ1=sQuery(id+"F0.wireOp",EDGE,"E1");var subQ2=makeQuery(id+"F0.imprint","INTERSECT",VERTEX,{"derivedFrom":[subQ1,subQ0]});Q4=makeQuery(id+"F0.imprint","IMPRINT",FACE,{"disambiguationData":[TD([[makeQuery(id+"F0.imprint","IMPRINT",EDGE,{"disambiguationData":[TD([[subQ2,-1.0]])],"derivedFrom":subQ0}),1.0]])]});}
            var Q5;
            {var subQ0=sQuery(id+"F0.wireOp",EDGE,"E18.2.0");var subQ1=sQuery(id+"F0.wireOp",EDGE,"E1");var subQ2=makeQuery(id+"F0.imprint","INTERSECT",VERTEX,{"derivedFrom":[subQ1,subQ0]});Q5=makeQuery(id+"F0.imprint","IMPRINT",FACE,{"disambiguationData":[TD([[makeQuery(id+"F0.imprint","IMPRINT",EDGE,{"disambiguationData":[TD([[subQ2,-1.0]])],"derivedFrom":subQ0}),-1.0]])]});}
            var Q6;
            {var subQ0=sQuery(id+"F0.wireOp",EDGE,"E18.1.0");var subQ1=sQuery(id+"F0.wireOp",EDGE,"E1");var subQ2=makeQuery(id+"F0.imprint","INTERSECT",VERTEX,{"derivedFrom":[subQ1,subQ0]});Q6=makeQuery(id+"F0.imprint","IMPRINT",FACE,{"disambiguationData":[TD([[makeQuery(id+"F0.imprint","IMPRINT",EDGE,{"disambiguationData":[TD([[subQ2,1.0]])],"derivedFrom":subQ1}),1.0]])]});}
            var Q7;
            {var subQ0=sQuery(id+"F0.wireOp",EDGE,"E18.2.0");var subQ1=sQuery(id+"F0.wireOp",EDGE,"E1");var subQ2=makeQuery(id+"F0.imprint","INTERSECT",VERTEX,{"derivedFrom":[subQ1,subQ0]});Q7=makeQuery(id+"F0.imprint","IMPRINT",FACE,{"disambiguationData":[TD([[makeQuery(id+"F0.imprint","IMPRINT",EDGE,{"disambiguationData":[TD([[subQ2,1.0]])],"derivedFrom":subQ1}),1.0]])]});}
            var Q8;
            {var subQ0=sQuery(id+"F0.wireOp",EDGE,"E6");var subQ1=sQuery(id+"F0.wireOp",EDGE,"E1");var subQ2=makeQuery(id+"F0.imprint","INTERSECT",VERTEX,{"derivedFrom":[subQ1,subQ0]});Q8=makeQuery(id+"F0.imprint","IMPRINT",FACE,{"disambiguationData":[TD([[makeQuery(id+"F0.imprint","IMPRINT",EDGE,{"disambiguationData":[TD([[subQ2,1.0]])],"derivedFrom":subQ1}),1.0]])]});}
            extrude(context, id + "F2", {"entities" : qUnion([Q0, Q1, Q2, Q3, Q4, Q5, Q6, Q7, Q8]), "operationType" : NewBodyOperationType.ADD, "depth" : 220 * mm, "offsetDistance" : 25 * mm});
        }
        {
            var Q0;
            {var subQ5=sQuery(id+"F0.wireOp",EDGE,"G2edZedI-oMVv-zGGG-3rpf-8qc5Rzpi7jZh.bottom");Q0=makeQuery(id+"F0.imprint","IMPRINT",FACE,{"disambiguationData":[TD([[makeQuery(id+"F0.imprint","IMPRINT",EDGE,{"derivedFrom":subQ5}),1.0]])]});}
            var Q1;
            {var subQ0=sQuery(id+"F0.wireOp",EDGE,"G2edZedI-oMVv-zGGG-3rpf-8qc5Rzpi7jZh.left");var subQ1=sQuery(id+"F0.wireOp",EDGE,"MHhcaKt2-idaq-ussF-yxv1-Ysw6X7YejIML.top");var subQ2=makeQuery(id+"F0.imprint","INTERSECT",VERTEX,{"derivedFrom":[subQ1,subQ0]});Q1=makeQuery(id+"F0.imprint","IMPRINT",FACE,{"disambiguationData":[TD([[makeQuery(id+"F0.imprint","IMPRINT",EDGE,{"disambiguationData":[TD([[subQ2,-1.0]])],"derivedFrom":subQ1}),-1.0]])]});}
            var Q2;
            {var subQ0=sQuery(id+"F0.wireOp",EDGE,"G2edZedI-oMVv-zGGG-3rpf-8qc5Rzpi7jZh.left");var subQ1=sQuery(id+"F0.wireOp",EDGE,"MHhcaKt2-idaq-ussF-yxv1-Ysw6X7YejIML.top");var subQ2=makeQuery(id+"F0.imprint","INTERSECT",VERTEX,{"derivedFrom":[subQ1,subQ0]});Q2=makeQuery(id+"F0.imprint","IMPRINT",FACE,{"disambiguationData":[TD([[makeQuery(id+"F0.imprint","IMPRINT",EDGE,{"disambiguationData":[TD([[subQ2,-1.0]])],"derivedFrom":subQ1}),1.0]])]});}
            var Q3;
            {var subQ0=sQuery(id+"F0.wireOp",EDGE,"G2edZedI-oMVv-zGGG-3rpf-8qc5Rzpi7jZh.left");var subQ1=sQuery(id+"F0.wireOp",EDGE,"UooLEnTI-Uf4f-MH2r-6JwD-Mf36DO2BtYOc.bottom");var subQ2=makeQuery(id+"F0.imprint","INTERSECT",VERTEX,{"derivedFrom":[subQ1,subQ0]});Q3=makeQuery(id+"F0.imprint","IMPRINT",FACE,{"disambiguationData":[TD([[makeQuery(id+"F0.imprint","IMPRINT",EDGE,{"disambiguationData":[TD([[subQ2,-1.0]])],"derivedFrom":subQ1}),1.0]])]});}
            var Q4;
            {var subQ0=sQuery(id+"F0.wireOp",EDGE,"G2edZedI-oMVv-zGGG-3rpf-8qc5Rzpi7jZh.left");var subQ1=sQuery(id+"F0.wireOp",EDGE,"MHhcaKt2-idaq-ussF-yxv1-Ysw6X7YejIML.bottom");var subQ2=makeQuery(id+"F0.imprint","INTERSECT",VERTEX,{"derivedFrom":[subQ1,subQ0]});Q4=makeQuery(id+"F0.imprint","IMPRINT",FACE,{"disambiguationData":[TD([[makeQuery(id+"F0.imprint","IMPRINT",EDGE,{"disambiguationData":[TD([[subQ2,-1.0]])],"derivedFrom":subQ1}),-1.0]])]});}
            var Q5;
            {var subQ0=sQuery(id+"F0.wireOp",EDGE,"G2edZedI-oMVv-zGGG-3rpf-8qc5Rzpi7jZh.left");var subQ1=sQuery(id+"F0.wireOp",EDGE,"MHhcaKt2-idaq-ussF-yxv1-Ysw6X7YejIML.bottom");var subQ2=makeQuery(id+"F0.imprint","INTERSECT",VERTEX,{"derivedFrom":[subQ1,subQ0]});Q5=makeQuery(id+"F0.imprint","IMPRINT",FACE,{"disambiguationData":[TD([[makeQuery(id+"F0.imprint","IMPRINT",EDGE,{"disambiguationData":[TD([[subQ2,-1.0]])],"derivedFrom":subQ1}),1.0]])]});}
            var Q6;
            {var subQ5=sQuery(id+"F0.wireOp",EDGE,"G2edZedI-oMVv-zGGG-3rpf-8qc5Rzpi7jZh.top");Q6=makeQuery(id+"F0.imprint","IMPRINT",FACE,{"disambiguationData":[TD([[makeQuery(id+"F0.imprint","IMPRINT",EDGE,{"derivedFrom":subQ5}),-1.0]])]});}
            var Q7;
            {var subQ5=sQuery(id+"F0.wireOp",EDGE,"UooLEnTI-Uf4f-MH2r-6JwD-Mf36DO2BtYOc.left");Q7=makeQuery(id+"F0.imprint","IMPRINT",FACE,{"disambiguationData":[TD([[makeQuery(id+"F0.imprint","IMPRINT",EDGE,{"derivedFrom":subQ5}),-1.0]])]});}
            var Q8;
            {var subQ5=sQuery(id+"F0.wireOp",EDGE,"UooLEnTI-Uf4f-MH2r-6JwD-Mf36DO2BtYOc.right");Q8=makeQuery(id+"F0.imprint","IMPRINT",FACE,{"disambiguationData":[TD([[makeQuery(id+"F0.imprint","IMPRINT",EDGE,{"derivedFrom":subQ5}),1.0]])]});}
            var Q9;
            {var subQ0=sQuery(id+"F0.wireOp",EDGE,"03e8Ckts-ZFi5-Aq3V-xVUe-yBUDc2XyNOQ6");Q9=makeQuery(id+"F0.imprint","IMPRINT",FACE,{"disambiguationData":[TD([[makeQuery(id+"F0.imprint","IMPRINT",EDGE,{"derivedFrom":subQ0}),1.0]])]});}
            var Q10;
            {var subQ0=sQuery(id+"F0.wireOp",EDGE,"bj91yUHZ-Wt7Y-C2vt-p8Xj-VTrvMNZv7KkJ");Q10=makeQuery(id+"F0.imprint","IMPRINT",FACE,{"disambiguationData":[TD([[makeQuery(id+"F0.imprint","IMPRINT",EDGE,{"derivedFrom":subQ0}),-1.0]])]});}
            var Q11;
            {var subQ0=sQuery(id+"F0.wireOp",EDGE,"UsHAKyTv-6jtb-spoe-rsad-w7DXaWFApGhJ");Q11=makeQuery(id+"F0.imprint","IMPRINT",FACE,{"disambiguationData":[TD([[makeQuery(id+"F0.imprint","IMPRINT",EDGE,{"derivedFrom":subQ0}),1.0]])]});}
            var Q12;
            {var subQ5=sQuery(id+"F0.wireOp",EDGE,"U6Gb84Ca-BoU4-zACI-EIev-EI8B9hxLx2hd.bottom");Q12=makeQuery(id+"F0.imprint","IMPRINT",FACE,{"disambiguationData":[TD([[makeQuery(id+"F0.imprint","IMPRINT",EDGE,{"derivedFrom":subQ5}),-1.0]])]});}
            var Q13;
            {var subQ5=sQuery(id+"F0.wireOp",EDGE,"KJFaWd3U-YvpL-C540-iaLV-ns6R3owsW4g9.left");Q13=makeQuery(id+"F0.imprint","IMPRINT",FACE,{"disambiguationData":[TD([[makeQuery(id+"F0.imprint","IMPRINT",EDGE,{"derivedFrom":subQ5}),1.0]])]});}
            var Q14;
            {var subQ5=sQuery(id+"F0.wireOp",EDGE,"WVTM5ykO-ORzQ-6imj-rCBD-ZudhNr8kMxeS.bottom");Q14=makeQuery(id+"F0.imprint","IMPRINT",FACE,{"disambiguationData":[TD([[makeQuery(id+"F0.imprint","IMPRINT",EDGE,{"derivedFrom":subQ5}),1.0]])]});}
            var Q15;
            {var subQ5=sQuery(id+"F0.wireOp",EDGE,"YnwhtgPZ-tjwQ-rwOe-Yv9D-G0hxzTefPX9C.left");Q15=makeQuery(id+"F0.imprint","IMPRINT",FACE,{"disambiguationData":[TD([[makeQuery(id+"F0.imprint","IMPRINT",EDGE,{"derivedFrom":subQ5}),-1.0]])]});}
            var Q16;
            {var subQ0=sQuery(id+"F0.wireOp",EDGE,"3ec345ef-f0f0-4e93-9e5e-b6a35eb55933.1.15");var subQ1=sQuery(id+"F0.wireOp",EDGE,"G2edZedI-oMVv-zGGG-3rpf-8qc5Rzpi7jZh.right");var subQ2=makeQuery(id+"F0.imprint","INTERSECT",VERTEX,{"derivedFrom":[subQ1,subQ0]});Q16=makeQuery(id+"F0.imprint","IMPRINT",FACE,{"disambiguationData":[TD([[makeQuery(id+"F0.imprint","IMPRINT",EDGE,{"disambiguationData":[TD([[subQ2,-1.0]])],"derivedFrom":subQ1}),1.0]])]});}
            var Q17;
            {var subQ0=sQuery(id+"F0.wireOp",EDGE,"Fhyrr48q-6Ub6-qUJE-WvSH-lKAYv9wGpefs");var subQ1=sQuery(id+"F0.wireOp",EDGE,"G2edZedI-oMVv-zGGG-3rpf-8qc5Rzpi7jZh.right");var subQ2=makeQuery(id+"F0.imprint","INTERSECT",VERTEX,{"derivedFrom":[subQ1,subQ0]});Q17=makeQuery(id+"F0.imprint","IMPRINT",FACE,{"disambiguationData":[TD([[makeQuery(id+"F0.imprint","IMPRINT",EDGE,{"disambiguationData":[TD([[subQ2,1.0]])],"derivedFrom":subQ1}),1.0]])]});}
            var Q18;
            {var subQ0=sQuery(id+"F0.wireOp",EDGE,"Fhyrr48q-6Ub6-qUJE-WvSH-lKAYv9wGpefs");var subQ1=sQuery(id+"F0.wireOp",EDGE,"G2edZedI-oMVv-zGGG-3rpf-8qc5Rzpi7jZh.right");var subQ2=makeQuery(id+"F0.imprint","INTERSECT",VERTEX,{"derivedFrom":[subQ1,subQ0]});Q18=makeQuery(id+"F0.imprint","IMPRINT",FACE,{"disambiguationData":[TD([[makeQuery(id+"F0.imprint","IMPRINT",EDGE,{"disambiguationData":[TD([[subQ2,1.0]])],"derivedFrom":subQ1}),-1.0]])]});}
            var Q19;
            {var subQ0=sQuery(id+"F0.wireOp",EDGE,"Fhyrr48q-6Ub6-qUJE-WvSH-lKAYv9wGpefs");var subQ1=sQuery(id+"F0.wireOp",EDGE,"G2edZedI-oMVv-zGGG-3rpf-8qc5Rzpi7jZh.left");var subQ2=makeQuery(id+"F0.imprint","INTERSECT",VERTEX,{"derivedFrom":[subQ1,subQ0]});Q19=makeQuery(id+"F0.imprint","IMPRINT",FACE,{"disambiguationData":[TD([[makeQuery(id+"F0.imprint","IMPRINT",EDGE,{"disambiguationData":[TD([[subQ2,1.0]])],"derivedFrom":subQ1}),-1.0]])]});}
            var Q20;
            {var subQ0=sQuery(id+"F0.wireOp",EDGE,"3ec345ef-f0f0-4e93-9e5e-b6a35eb55933.2.15");var subQ1=sQuery(id+"F0.wireOp",EDGE,"G2edZedI-oMVv-zGGG-3rpf-8qc5Rzpi7jZh.left");var subQ2=makeQuery(id+"F0.imprint","INTERSECT",VERTEX,{"derivedFrom":[subQ1,subQ0]});Q20=makeQuery(id+"F0.imprint","IMPRINT",FACE,{"disambiguationData":[TD([[makeQuery(id+"F0.imprint","IMPRINT",EDGE,{"disambiguationData":[TD([[subQ2,-1.0]])],"derivedFrom":subQ1}),-1.0]])]});}
            var Q21;
            {var subQ0=sQuery(id+"F0.wireOp",EDGE,"Fhyrr48q-6Ub6-qUJE-WvSH-lKAYv9wGpefs");var subQ1=sQuery(id+"F0.wireOp",EDGE,"G2edZedI-oMVv-zGGG-3rpf-8qc5Rzpi7jZh.left");var subQ2=makeQuery(id+"F0.imprint","INTERSECT",VERTEX,{"derivedFrom":[subQ1,subQ0]});Q21=makeQuery(id+"F0.imprint","IMPRINT",FACE,{"disambiguationData":[TD([[makeQuery(id+"F0.imprint","IMPRINT",EDGE,{"disambiguationData":[TD([[subQ2,1.0]])],"derivedFrom":subQ1}),1.0]])]});}
            var Q22;
            {var subQ0=sQuery(id+"F0.wireOp",EDGE,"3ec345ef-f0f0-4e93-9e5e-b6a35eb55933.1.15");var subQ1=sQuery(id+"F0.wireOp",EDGE,"3ec345ef-f0f0-4e93-9e5e-b6a35eb55933.1.2");var subQ2=makeQuery(id+"F0.imprint","INTERSECT",VERTEX,{"derivedFrom":[subQ1,subQ0]});Q22=makeQuery(id+"F0.imprint","IMPRINT",FACE,{"disambiguationData":[TD([[makeQuery(id+"F0.imprint","IMPRINT",EDGE,{"disambiguationData":[TD([[subQ2,1.0]])],"derivedFrom":subQ1}),-1.0]])]});}
            var Q23;
            {var subQ0=sQuery(id+"F0.wireOp",EDGE,"3ec345ef-f0f0-4e93-9e5e-b6a35eb55933.1.15");var subQ1=sQuery(id+"F0.wireOp",EDGE,"3ec345ef-f0f0-4e93-9e5e-b6a35eb55933.1.2");var subQ2=makeQuery(id+"F0.imprint","INTERSECT",VERTEX,{"derivedFrom":[subQ1,subQ0]});Q23=makeQuery(id+"F0.imprint","IMPRINT",FACE,{"disambiguationData":[TD([[makeQuery(id+"F0.imprint","IMPRINT",EDGE,{"disambiguationData":[TD([[subQ2,1.0]])],"derivedFrom":subQ1}),1.0]])]});}
            var Q24;
            {var subQ0=sQuery(id+"F0.wireOp",EDGE,"3ec345ef-f0f0-4e93-9e5e-b6a35eb55933.2.15");var subQ1=sQuery(id+"F0.wireOp",EDGE,"3ec345ef-f0f0-4e93-9e5e-b6a35eb55933.1.2");var subQ2=makeQuery(id+"F0.imprint","INTERSECT",VERTEX,{"derivedFrom":[subQ1,subQ0]});Q24=makeQuery(id+"F0.imprint","IMPRINT",FACE,{"disambiguationData":[TD([[makeQuery(id+"F0.imprint","IMPRINT",EDGE,{"disambiguationData":[TD([[subQ2,-1.0]])],"derivedFrom":subQ1}),1.0]])]});}
            var Q25;
            {var subQ5=sQuery(id+"F0.wireOp",EDGE,"3ec345ef-f0f0-4e93-9e5e-b6a35eb55933.1.17");Q25=makeQuery(id+"F0.imprint","IMPRINT",FACE,{"disambiguationData":[TD([[makeQuery(id+"F0.imprint","IMPRINT",EDGE,{"derivedFrom":subQ5}),1.0]])]});}
            var Q26;
            {var subQ5=sQuery(id+"F0.wireOp",EDGE,"3ec345ef-f0f0-4e93-9e5e-b6a35eb55933.2.17");Q26=makeQuery(id+"F0.imprint","IMPRINT",FACE,{"disambiguationData":[TD([[makeQuery(id+"F0.imprint","IMPRINT",EDGE,{"derivedFrom":subQ5}),1.0]])]});}
            var Q27;
            {var subQ0=sQuery(id+"F0.wireOp",EDGE,"U6Gb84Ca-BoU4-zACI-EIev-EI8B9hxLx2hd.bottom");Q27=makeQuery(id+"F0.imprint","IMPRINT",FACE,{"disambiguationData":[TD([[makeQuery(id+"F0.imprint","IMPRINT",EDGE,{"derivedFrom":subQ0}),1.0]])]});}
            var Q28;
            {var subQ0=sQuery(id+"F0.wireOp",EDGE,"U6Gb84Ca-BoU4-zACI-EIev-EI8B9hxLx2hd.top");Q28=makeQuery(id+"F0.imprint","IMPRINT",FACE,{"disambiguationData":[TD([[makeQuery(id+"F0.imprint","IMPRINT",EDGE,{"derivedFrom":subQ0}),-1.0]])]});}
            var Q29;
            {var subQ3=sQuery(id+"F0.wireOp",EDGE,"3ec345ef-f0f0-4e93-9e5e-b6a35eb55933.1.11");Q29=makeQuery(id+"F0.imprint","IMPRINT",FACE,{"disambiguationData":[TD([[makeQuery(id+"F0.imprint","IMPRINT",EDGE,{"derivedFrom":subQ3}),-1.0]])]});}
            var Q30;
            {var subQ2=sQuery(id+"F0.wireOp",EDGE,"3ec345ef-f0f0-4e93-9e5e-b6a35eb55933.1.11");Q30=makeQuery(id+"F0.imprint","IMPRINT",FACE,{"disambiguationData":[TD([[makeQuery(id+"F0.imprint","IMPRINT",EDGE,{"derivedFrom":subQ2}),1.0]])]});}
            var Q31;
            {var subQ3=sQuery(id+"F0.wireOp",EDGE,"3ec345ef-f0f0-4e93-9e5e-b6a35eb55933.2.11");Q31=makeQuery(id+"F0.imprint","IMPRINT",FACE,{"disambiguationData":[TD([[makeQuery(id+"F0.imprint","IMPRINT",EDGE,{"derivedFrom":subQ3}),-1.0]])]});}
            var Q32;
            {var subQ2=sQuery(id+"F0.wireOp",EDGE,"3ec345ef-f0f0-4e93-9e5e-b6a35eb55933.2.11");Q32=makeQuery(id+"F0.imprint","IMPRINT",FACE,{"disambiguationData":[TD([[makeQuery(id+"F0.imprint","IMPRINT",EDGE,{"derivedFrom":subQ2}),1.0]])]});}
            var Q33;
            {var subQ3=sQuery(id+"F0.wireOp",EDGE,"E2");var subQ13=sQuery(id+"F0.wireOp",EDGE,"E7");var subQ14=makeQuery(id+"F0.imprint","INTERSECT",VERTEX,{"derivedFrom":[subQ3,subQ13]});Q33=makeQuery(id+"F0.imprint","IMPRINT",FACE,{"disambiguationData":[TD([[makeQuery(id+"F0.imprint","IMPRINT",EDGE,{"disambiguationData":[TD([[subQ14,-1.0]])],"derivedFrom":subQ3}),1.0]])]});}
            var Q34;
            {var subQ0=sQuery(id+"F0.wireOp",EDGE,"E7");var subQ1=sQuery(id+"F0.wireOp",EDGE,"E2");var subQ2=makeQuery(id+"F0.imprint","INTERSECT",VERTEX,{"derivedFrom":[subQ1,subQ0]});Q34=makeQuery(id+"F0.imprint","IMPRINT",FACE,{"disambiguationData":[TD([[makeQuery(id+"F0.imprint","IMPRINT",EDGE,{"disambiguationData":[TD([[subQ2,-1.0]])],"derivedFrom":subQ1}),-1.0]])]});}
            var Q35;
            {var subQ0=sQuery(id+"F0.wireOp",EDGE,"E18.1.1");var subQ1=sQuery(id+"F0.wireOp",EDGE,"E2");var subQ2=makeQuery(id+"F0.imprint","INTERSECT",VERTEX,{"derivedFrom":[subQ1,subQ0]});Q35=makeQuery(id+"F0.imprint","IMPRINT",FACE,{"disambiguationData":[TD([[makeQuery(id+"F0.imprint","IMPRINT",EDGE,{"disambiguationData":[TD([[subQ2,-1.0]])],"derivedFrom":subQ1}),-1.0]])]});}
            var Q36;
            {var subQ0=sQuery(id+"F0.wireOp",EDGE,"E18.2.1");var subQ1=sQuery(id+"F0.wireOp",EDGE,"E2");var subQ2=makeQuery(id+"F0.imprint","INTERSECT",VERTEX,{"derivedFrom":[subQ1,subQ0]});Q36=makeQuery(id+"F0.imprint","IMPRINT",FACE,{"disambiguationData":[TD([[makeQuery(id+"F0.imprint","IMPRINT",EDGE,{"disambiguationData":[TD([[subQ2,-1.0]])],"derivedFrom":subQ1}),-1.0]])]});}
            extrude(context, id + "F3", {"entities" : qUnion([Q0, Q1, Q2, Q3, Q4, Q5, Q6, Q7, Q8, Q9, Q10, Q11, Q12, Q13, Q14, Q15, Q16, Q17, Q18, Q19, Q20, Q21, Q22, Q23, Q24, Q25, Q26, Q27, Q28, Q29, Q30, Q31, Q32, Q33, Q34, Q35, Q36]), "operationType" : NewBodyOperationType.ADD, "depth" : 235 * mm, "offsetDistance" : 25 * mm});
        }
        {
            var Q0;
            Q0=makeQuery(id+"F3.opExtrude","CAP_EDGE",EDGE,{"disambiguationData":[OSD([sQuery(id+"F0.wireOp",EDGE,"E18.2.8")])],"isStart":false});
            var Q1;
            Q1=makeQuery(id+"F3.opExtrude","CAP_EDGE",EDGE,{"disambiguationData":[OSD([sQuery(id+"F0.wireOp",EDGE,"E18.1.8")])],"isStart":false});
            var Q2;
            Q2=makeQuery(id+"F3.opExtrude","CAP_EDGE",EDGE,{"disambiguationData":[OSD([sQuery(id+"F0.wireOp",EDGE,"E17")])],"isStart":false});
            chamfer(context, id + "F4", {"entities" : qUnion([Q0, Q1, Q2]), "chamferType" : ChamferType.OFFSET_ANGLE, "width" : 15 * mm, "oppositeDirection" : false, "angle" : 75 * degree, "tangentPropagation" : true});
        }
        {
            var Q0;
            {var subQ0=sQuery(id+"F0.wireOp",EDGE,"ARnEnpE5-tkmW-Q9Fp-N7HQ-ZdpaRJQSmeqH.bottom");var subQ1=sQuery(id+"F0.wireOp",EDGE,"E1");Q0=makeQuery(id+"F2.opExtrude","CAP_EDGE",EDGE,{"disambiguationData":[OSD([subQ1]),TDD([makeQuery(id+"F0.imprint","IMPRINT",EDGE,{"disambiguationData":[TD([[makeQuery(id+"F0.imprint","INTERSECT",VERTEX,{"derivedFrom":[subQ1,subQ0,sQuery(id+"F0.wireOp",EDGE,"ARnEnpE5-tkmW-Q9Fp-N7HQ-ZdpaRJQSmeqH.left"),sQuery(id+"F0.wireOp",EDGE,"UsHAKyTv-6jtb-spoe-rsad-w7DXaWFApGhJ")]}),-1.0]])],"derivedFrom":subQ1})])],"isStart":false});}
            var Q1;
            {var subQ0=sQuery(id+"F0.wireOp",EDGE,"fYTYB3PY-5dvC-i0FG-IhBz-imLdNv0oFj73.left");var subQ1=sQuery(id+"F0.wireOp",EDGE,"E1");Q1=makeQuery(id+"F2.opExtrude","CAP_EDGE",EDGE,{"disambiguationData":[OSD([subQ1]),TDD([makeQuery(id+"F0.imprint","IMPRINT",EDGE,{"disambiguationData":[TD([[makeQuery(id+"F0.imprint","INTERSECT",VERTEX,{"derivedFrom":[subQ1,sQuery(id+"F0.wireOp",EDGE,"fYTYB3PY-5dvC-i0FG-IhBz-imLdNv0oFj73.bottom"),subQ0,sQuery(id+"F0.wireOp",EDGE,"kZxKVhXT-tHgl-xRPm-lkcx-u0khmLZUqcnL")]}),1.0]])],"derivedFrom":subQ1})])],"isStart":false});}
            var Q2;
            {var subQ0=sQuery(id+"F0.wireOp",EDGE,"JRACFuVa-LFQl-MoOF-o5kD-FoGYgOgg0vGQ.bottom");var subQ1=sQuery(id+"F0.wireOp",EDGE,"E1");Q2=makeQuery(id+"F2.opExtrude","CAP_EDGE",EDGE,{"disambiguationData":[OSD([subQ1]),TDD([makeQuery(id+"F0.imprint","IMPRINT",EDGE,{"disambiguationData":[TD([[makeQuery(id+"F0.imprint","INTERSECT",VERTEX,{"derivedFrom":[subQ1,subQ0,sQuery(id+"F0.wireOp",EDGE,"JRACFuVa-LFQl-MoOF-o5kD-FoGYgOgg0vGQ.left"),sQuery(id+"F0.wireOp",EDGE,"CjHSthgf-UrMd-mykl-wSX2-3saethCeIdIi")]}),1.0]])],"derivedFrom":subQ1})])],"isStart":false});}
            var Q3;
            {var subQ0=sQuery(id+"F0.wireOp",EDGE,"qvxIDn41-u5vC-3tcf-A1ba-gfAf9TCSAjBw.left");var subQ1=sQuery(id+"F0.wireOp",EDGE,"E1");Q3=makeQuery(id+"F2.opExtrude","CAP_EDGE",EDGE,{"disambiguationData":[OSD([subQ1]),TDD([makeQuery(id+"F0.imprint","IMPRINT",EDGE,{"disambiguationData":[TD([[makeQuery(id+"F0.imprint","INTERSECT",VERTEX,{"derivedFrom":[subQ1,sQuery(id+"F0.wireOp",EDGE,"qvxIDn41-u5vC-3tcf-A1ba-gfAf9TCSAjBw.bottom"),subQ0,sQuery(id+"F0.wireOp",EDGE,"A8od2ZFF-7y6o-rShD-bBN7-uJ0yuPEPxqf4")]}),-1.0]])],"derivedFrom":subQ1})])],"isStart":false});}
            var Q4;
            {var subQ0=sQuery(id+"F0.wireOp",EDGE,"E1");Q4=makeQuery(id+"F3.opExtrude","CAP_EDGE",EDGE,{"disambiguationData":[OSD([subQ0]),TDD([makeQuery(id+"F0.imprint","IMPRINT",EDGE,{"disambiguationData":[TD([[makeQuery(id+"F0.imprint","INTERSECT",VERTEX,{"derivedFrom":[subQ0,sQuery(id+"F0.wireOp",EDGE,"E18.1.0")]}),1.0]])],"derivedFrom":subQ0})])],"isStart":false});}
            var Q5;
            {var subQ0=sQuery(id+"F0.wireOp",EDGE,"E1");Q5=makeQuery(id+"F3.opExtrude","CAP_EDGE",EDGE,{"disambiguationData":[OSD([subQ0]),TDD([makeQuery(id+"F0.imprint","IMPRINT",EDGE,{"disambiguationData":[TD([[makeQuery(id+"F0.imprint","INTERSECT",VERTEX,{"derivedFrom":[subQ0,sQuery(id+"F0.wireOp",EDGE,"E18.2.0")]}),1.0]])],"derivedFrom":subQ0})])],"isStart":false});}
            var Q6;
            {var subQ0=sQuery(id+"F0.wireOp",EDGE,"E1");Q6=makeQuery(id+"F3.opExtrude","CAP_EDGE",EDGE,{"disambiguationData":[OSD([subQ0]),TDD([makeQuery(id+"F0.imprint","IMPRINT",EDGE,{"disambiguationData":[TD([[makeQuery(id+"F0.imprint","INTERSECT",VERTEX,{"derivedFrom":[subQ0,sQuery(id+"F0.wireOp",EDGE,"E6")]}),1.0]])],"derivedFrom":subQ0})])],"isStart":false});}
            fillet(context, id + "F5", {"entities" : qUnion([Q0, Q1, Q2, Q3, Q4, Q5, Q6]), "radius" : 6 * mm, "tangentPropagation" : true, "allowEdgeOverflow" : false});
        }
        {
            var Q0;
            Q0=makeQuery(id+"F0.imprint","IMPRINT",FACE,{"disambiguationData":[TD([[makeQuery(id+"F0.imprint","IMPRINT",EDGE,{"derivedFrom":sQuery(id+"F0.wireOp",EDGE,"E11")}),1.0]])]});
            var Q1;
            Q1=makeQuery(id+"F0.imprint","IMPRINT",FACE,{"disambiguationData":[TD([[makeQuery(id+"F0.imprint","IMPRINT",EDGE,{"derivedFrom":sQuery(id+"F0.wireOp",EDGE,"E13.1.0")}),-1.0]])]});
            var Q2;
            Q2=makeQuery(id+"F0.imprint","IMPRINT",FACE,{"disambiguationData":[TD([[makeQuery(id+"F0.imprint","IMPRINT",EDGE,{"derivedFrom":sQuery(id+"F0.wireOp",EDGE,"E13.2.0")}),-1.0]])]});
            extrude(context, id + "F6", {"entities" : qUnion([Q0, Q1, Q2]), "operationType" : NewBodyOperationType.ADD, "depth" : 3 * mm, "offsetDistance" : 25 * mm});
        }
        {
            var Q0;
            {var subQ4=sQuery(id+"F0.wireOp",EDGE,"E18.1.4");Q0=makeQuery(id+"F0.imprint","IMPRINT",FACE,{"disambiguationData":[TD([[makeQuery(id+"F0.imprint","IMPRINT",EDGE,{"derivedFrom":subQ4}),1.0]])]});}
            var Q1;
            {var subQ2=sQuery(id+"F0.wireOp",EDGE,"E18.2.4");Q1=makeQuery(id+"F0.imprint","IMPRINT",FACE,{"disambiguationData":[TD([[makeQuery(id+"F0.imprint","IMPRINT",EDGE,{"derivedFrom":subQ2}),1.0]])]});}
            var Q2;
            {var subQ2=sQuery(id+"F0.wireOp",EDGE,"E8");Q2=makeQuery(id+"F0.imprint","IMPRINT",FACE,{"disambiguationData":[TD([[makeQuery(id+"F0.imprint","IMPRINT",EDGE,{"derivedFrom":subQ2}),1.0]])]});}
            extrude(context, id + "F7", {"entities" : qUnion([Q0, Q1, Q2]), "operationType" : NewBodyOperationType.ADD, "depth" : 30 * mm, "offsetDistance" : 25 * mm});
        }
        {
            var Q0;
            Q0=qCreatedBy(makeId("Top.planeOp"),FACE);
            var sketch = newSketch(context, id + "F8", { "sketchPlane" : qUnion([Q0])});
            skLineSegment(sketch, "E20.bottom", {"start": v(100, 100) * mm, "end": v(-100, 100) * mm});
            skLineSegment(sketch, "E20.top", {"start": v(100, -100) * mm, "end": v(-100, -100) * mm});
            skLineSegment(sketch, "E20.left", {"start": v(100, 100) * mm, "end": v(100, -100) * mm});
            skLineSegment(sketch, "E20.right", {"start": v(-100, 100) * mm, "end": v(-100, -100) * mm});
            skPoint(sketch, "E20.middle", {"position": v(0, 0) * mm});
            skSolve(sketch);
        }
        {
            var Q0;
            Q0=makeQuery(id+"F8.imprint","IMPRINT",FACE,{"disambiguationData":[TD([[makeQuery(id+"F8.imprint","IMPRINT",EDGE,{"derivedFrom":sQuery(id+"F8.wireOp",EDGE,"E20.bottom")}),1.0]])]});
            extrude(context, id + "F9", {"entities" : qUnion([Q0]), "operationType" : NewBodyOperationType.ADD, "oppositeDirection" : true, "depth" : 20 * mm, "offsetDistance" : 25 * mm});
        }
        {
            var Q0;
            Q0=makeQuery(id+"F9.opExtrude","SWEPT_EDGE",EDGE,{"disambiguationData":[OSD([sQuery(id+"F8.wireOp",EDGE,"E20.top"),sQuery(id+"F8.wireOp",EDGE,"E20.right")])]});
            var Q1;
            Q1=makeQuery(id+"F9.opExtrude","SWEPT_EDGE",EDGE,{"disambiguationData":[OSD([sQuery(id+"F8.wireOp",EDGE,"E20.top"),sQuery(id+"F8.wireOp",EDGE,"E20.left")])]});
            var Q2;
            Q2=makeQuery(id+"F9.opExtrude","SWEPT_EDGE",EDGE,{"disambiguationData":[OSD([sQuery(id+"F8.wireOp",EDGE,"E20.bottom"),sQuery(id+"F8.wireOp",EDGE,"E20.left")])]});
            var Q3;
            Q3=makeQuery(id+"F9.opExtrude","SWEPT_EDGE",EDGE,{"disambiguationData":[OSD([sQuery(id+"F8.wireOp",EDGE,"E20.bottom"),sQuery(id+"F8.wireOp",EDGE,"E20.right")])]});
            fillet(context, id + "F10", {"entities" : qUnion([Q0, Q1, Q2, Q3]), "radius" : 5 * mm, "tangentPropagation" : true, "allowEdgeOverflow" : false});
        }
        {
            var Q0;
            Q0=makeQuery(id+"F0.imprint","IMPRINT",FACE,{"disambiguationData":[TD([[makeQuery(id+"F0.imprint","IMPRINT",EDGE,{"derivedFrom":sQuery(id+"F0.wireOp",EDGE,"E19.sketch_text.stroke-0")}),-1.0]])]});
            var Q1;
            Q1=makeQuery(id+"F0.imprint","IMPRINT",FACE,{"disambiguationData":[TD([[makeQuery(id+"F0.imprint","IMPRINT",EDGE,{"derivedFrom":sQuery(id+"F0.wireOp",EDGE,"E19.sketch_text.stroke-6")}),-1.0]])]});
            var Q2;
            Q2=makeQuery(id+"F0.imprint","IMPRINT",FACE,{"disambiguationData":[TD([[makeQuery(id+"F0.imprint","IMPRINT",EDGE,{"derivedFrom":sQuery(id+"F0.wireOp",EDGE,"E19.sketch_text.stroke-24")}),-1.0]])]});
            var Q3;
            Q3=makeQuery(id+"F0.imprint","IMPRINT",FACE,{"disambiguationData":[TD([[makeQuery(id+"F0.imprint","IMPRINT",EDGE,{"derivedFrom":sQuery(id+"F0.wireOp",EDGE,"E19.sketch_text.stroke-49")}),-1.0]])]});
            extrude(context, id + "F11", {"entities" : qUnion([Q0, Q1, Q2, Q3]), "operationType" : NewBodyOperationType.ADD, "depth" : 1 * mm, "offsetDistance" : 25 * mm});
        }
    });
